# Revit family: DC_Rheem_PLM_Raypak_B2404HWT
name_source: partatom
category: Plumbing Fixtures
revit_build: Autodesk Revit 2017 (Build: 20160225_1515(x64)
units: mm (PartAtom-declared; Revit-internal decimal feet)

## family parameters
Cut with Voids When Loaded = No
Host = Face
Part Type = Normal
Room Calculation Point = No
Round Connector Dimension = Use Radius
Shared = No

## types (4) — shared parameters
BaseHeight_ANZRS = 75 mm
BaseWidth_ANZRS = 75 mm
BoxHeight_ANZRS = 1195 mm  [stored 3.9206 ft]
ColdWaterPipeDiameter_ANZRS = 80 mm  [stored 0.262467 ft]
ColdWaterPipeDistance_ANZRS = 567 mm
ColdWaterPipeRadius_ANZRS = 40 mm  [stored 0.131234 ft]
ConnectionHeight_ANZRS = 910 mm
EleBoxHeightFromBase_ANZRS = 450 mm
EleBoxHeight_ANZRS = 380 mm  [stored 1.24672 ft]
EleBoxWidth_ANZRS = 160 mm
GasPipeDistance_ANZRS = 210 mm
GasPipeHeight_ANZRS = 600 mm
Height_ANZRS = 3210 mm
HotWaterPipeDiameter_ANZRS = 80 mm  [stored 0.262467 ft]
HotWaterPipeDistance_ANZRS = 235 mm
HotWaterPipeRadius_ANZRS = 40 mm  [stored 0.131234 ft]
Length_ANZRS = 1780 mm
Manufacturer = Raypak
Materials_ANZRS = Raypak - Grey Powder Coated Steel
PRVDiameter_ANZRS = 30 mm  [stored 0.0984252 ft]
PRVDistance_ANZRS = 400 mm
PRVRadius_ANZRS = 15 mm  [stored 0.0492126 ft]
TopBigDiameter_ANZRS = 1200 mm
TopH1_ANZRS = 300 mm
TopH2_ANZRS = 750 mm
TopSmallDiameter_ANZRS = 660 mm
URL = http://www.rheem.com.au
Width_ANZRS = 1430 mm
zero-valued in all types: BaseDistance_ANZRS, Default Elevation

## per-type parameters (varying)
| type | GasPipeDiameter_ANZRS | GasPipeRadius_ANZRS | Model | Type Comments |
| Raypak - Gas Water Heater- Outdoor - 2404 MJ/h  Natural gas, modulating gas control | 65 mm | 33 mm | B2404NCM/HWT | Recovery 9116L/h @ 50°C rise |
| Raypak - Gas Water Heater- Outdoor - 2404 MJ/h  Natural gas, On/Off gas control | 65 mm | 33 mm | B2404NCO/HWT | Recovery 9116L/h @ 50°C rise |
| Raypak - Gas Water Heater- Outdoor - 2530 MJ/h  Propane gas, modulating gas control | 40 mm  [stored 0.131234 ft] | 20 mm  [stored 0.0656168 ft] | B2404PCM/HWT | Recovery 9638L/h @ 50°C rise |
| Raypak - Gas Water Heater- Outdoor - 2530 MJ/h  Propane gas, On/Off gas control | 40 mm  [stored 0.131234 ft] | 20 mm  [stored 0.0656168 ft] | B2404PCO/HWT | Recovery 9638L/h @ 50°C rise |

note: column(s) folded — value = type name in every type: Description

note: [stored X ft] marks values corroborated as IEEE doubles in the binary element streams (Revit-internal decimal feet)

## geometry (parser evidence)
native form markers: Blend x6, Sweep x2
no freeform markers — native parametric forms only
